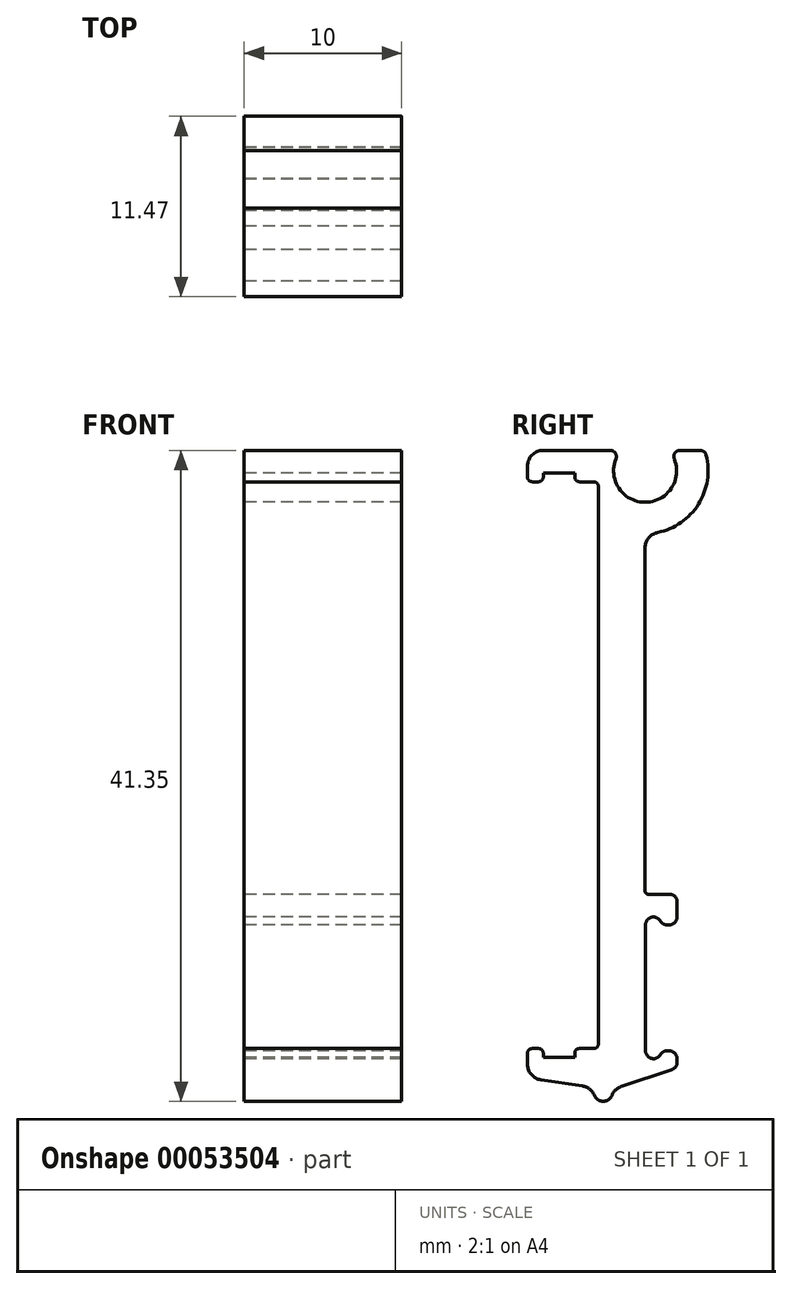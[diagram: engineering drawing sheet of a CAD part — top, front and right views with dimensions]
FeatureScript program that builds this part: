
annotation { "Feature Type Name" : "Feature", "Feature Type Description" : "" }
export const myFeature = defineFeature(function(context is Context, id is Id, definition is map)
    precondition{}
    {
        {
            var Q0;
            Q0=qCreatedBy(makeId("Right.planeOp"),FACE);
            var sketch = newSketch(context, id + "F0", { "sketchPlane" : qUnion([Q0])});
            skLineSegment(sketch, "E0.bottom", {"start": v(9.1, 40) * mm, "end": v(409.1, 40) * mm});
            skLineSegment(sketch, "E0.top", {"start": v(9.1, 21) * mm, "end": v(409.1, 21) * mm});
            skLineSegment(sketch, "E0.left", {"start": v(9.1, 40) * mm, "end": v(9.1, 21) * mm});
            skLineSegment(sketch, "E0.right", {"start": v(409.1, 40) * mm, "end": v(409.1, 21) * mm});
            skSolve(sketch);
        }
        {
            var Q0;
            Q0=qCreatedBy(makeId("Right.planeOp"),FACE);
            var sketch = newSketch(context, id + "F1", { "sketchPlane" : qUnion([Q0])});
            skLineSegment(sketch, "E1.bottom", {"start": v(-0.5, 35) * mm, "end": v(-4.5, 35) * mm});
            skLineSegment(sketch, "E1.top", {"start": v(-0.5, 0) * mm, "end": v(-4.5, 0) * mm});
            skLineSegment(sketch, "E1.left", {"start": v(0, 34.5) * mm, "end": v(0, 0.5) * mm});
            skLineSegment(sketch, "E1.right", {"start": v(-5, 34.5) * mm, "end": v(-5, 0.5) * mm});
            skPoint(sketch, "E2.visualSharp", {"position": v(0, 35) * mm});
            skArc(sketch, "E2.filletArc", {"start": v(0, 34.5) * mm, "mid": v(-0.15, 34.85) * mm, "end": v(-0.5, 35) * mm});
            skPoint(sketch, "E3.visualSharp", {"position": v(-5, 35) * mm});
            skArc(sketch, "E3.filletArc", {"start": v(-4.5, 35) * mm, "mid": v(-4.85, 34.85) * mm, "end": v(-5, 34.5) * mm});
            skPoint(sketch, "E4.visualSharp", {"position": v(-5, 0) * mm});
            skArc(sketch, "E4.filletArc", {"start": v(-5, 0.5) * mm, "mid": v(-4.85, 0.15) * mm, "end": v(-4.5, 0) * mm});
            skPoint(sketch, "E5.visualSharp", {"position": v(0, 0) * mm});
            skArc(sketch, "E5.filletArc", {"start": v(-0.5, 0) * mm, "mid": v(-0.15, 0.15) * mm, "end": v(0, 0.5) * mm});
            skLineSegment(sketch, "E6", {"start": v(-5, 17.5) * mm, "end": v(0, 17.5) * mm, "construction": true});
            skLineSegment(sketch, "E7.rect.bottom", {"start": v(-2.5, 36) * mm, "end": v(-2.5, 36) * mm});
            skLineSegment(sketch, "E7.rect.top", {"start": v(-1.5, 34) * mm, "end": v(-3.5, 34) * mm, "construction": true});
            skLineSegment(sketch, "E7.rect.left", {"start": v(-1.5, 35) * mm, "end": v(-1.5, 34) * mm, "construction": true});
            skLineSegment(sketch, "E7.rect.right", {"start": v(-3.5, 35) * mm, "end": v(-3.5, 34) * mm, "construction": true});
            skPoint(sketch, "E7.rect.middle", {"position": v(-2.5, 35) * mm});
            skPoint(sketch, "E8.visualSharp", {"position": v(-3.5, 36) * mm});
            skArc(sketch, "E8.filletArc", {"start": v(-2.5, 36) * mm, "mid": v(-3.2, 35.7) * mm, "end": v(-3.5, 35) * mm, "construction": true});
            skPoint(sketch, "E9.visualSharp", {"position": v(-1.5, 36) * mm});
            skArc(sketch, "E9.filletArc", {"start": v(-1.5, 35) * mm, "mid": v(-1.8, 35.7) * mm, "end": v(-2.5, 36) * mm, "construction": true});
            skPoint(sketch, "E10.MirrorP", {"position": v(-2.5, 0) * mm});
            skPoint(sketch, "E11.MirrorP", {"position": v(-1.5, -1) * mm});
            skArc(sketch, "E12.MirrorCS", {"start": v(-1.5, 0) * mm, "mid": v(-1.8, -0.7) * mm, "end": v(-2.5, -1) * mm, "construction": true});
            skPoint(sketch, "E13.MirrorP", {"position": v(-3.5, -1) * mm});
            skLineSegment(sketch, "E14.MirrorCS", {"start": v(-2.5, -1) * mm, "end": v(-2.5, -1) * mm});
            skArc(sketch, "E15.MirrorCS", {"start": v(-2.5, -1) * mm, "mid": v(-3.2, -0.7) * mm, "end": v(-3.5, 0) * mm, "construction": true});
            skLineSegment(sketch, "E16.MirrorCS", {"start": v(-3.5, 0) * mm, "end": v(-3.5, 1) * mm, "construction": true});
            skLineSegment(sketch, "E17.MirrorCS", {"start": v(-1.5, 1) * mm, "end": v(-3.5, 1) * mm, "construction": true});
            skLineSegment(sketch, "E18.MirrorCS", {"start": v(-1.5, 0) * mm, "end": v(-1.5, 1) * mm, "construction": true});
            skLineSegment(sketch, "E19.rect.bottom", {"start": v(-4.5, 29.4) * mm, "end": v(-5, 29.4) * mm});
            skLineSegment(sketch, "E19.rect.top", {"start": v(-4.5, 5.6) * mm, "end": v(-5, 5.6) * mm});
            skLineSegment(sketch, "E19.rect.left", {"start": v(-4.5, 29.4) * mm, "end": v(-4.5, 5.6) * mm, "construction": true});
            skPoint(sketch, "E19.rect.middle", {"position": v(-5, 17.5) * mm});
            skPoint(sketch, "E19.rect.right.end.orphan", {"position": v(-5.5, 5.6) * mm});
            skPoint(sketch, "E19.rect.right.start.orphan", {"position": v(-5.5, 29.4) * mm});
            skSolve(sketch);
        }
        {
            var Q0;
            Q0=qCreatedBy(makeId("Right.planeOp"),FACE);
            var sketch = newSketch(context, id + "F2", { "sketchPlane" : qUnion([Q0])});
            skLineSegment(sketch, "E20", {"start": v(-4.2, 35.5) * mm, "end": v(-3.8, 35.5) * mm});
            skLineSegment(sketch, "E21", {"start": v(0, 35.2) * mm, "end": v(0, -0.2) * mm});
            skLineSegment(sketch, "E22", {"start": v(-0.3, -0.5) * mm, "end": v(-1.2, -0.5) * mm});
            skLineSegment(sketch, "E23", {"start": v(-4.5, -0.8) * mm, "end": v(-4.5, -1.5) * mm});
            skLineSegment(sketch, "E24", {"start": v(-3.5, -2.5) * mm, "end": v(2.68, -2.5) * mm, "construction": true});
            skLineSegment(sketch, "E25", {"start": v(-4.5, 35.8) * mm, "end": v(-4.5, 36.5) * mm});
            skLineSegment(sketch, "E26", {"start": v(-3.5, 37.5) * mm, "end": v(0.74, 37.5) * mm});
            skLineSegment(sketch, "E27", {"start": v(-3.5, 35.8) * mm, "end": v(-3.5, 36.05) * mm});
            skLineSegment(sketch, "E28", {"start": v(-3.5, 36.05) * mm, "end": v(-1.5, 36.05) * mm});
            skLineSegment(sketch, "E29", {"start": v(-1.5, 36.05) * mm, "end": v(-1.5, 35.8) * mm});
            skLineSegment(sketch, "E30.trimOffspring", {"start": v(-1.2, 35.5) * mm, "end": v(-0.3, 35.5) * mm});
            skLineSegment(sketch, "E31.MirrorCS", {"start": v(-1.5, -1.05) * mm, "end": v(-1.5, -0.8) * mm});
            skLineSegment(sketch, "E32.MirrorCS", {"start": v(-3.5, -0.8) * mm, "end": v(-3.5, -1.05) * mm});
            skLineSegment(sketch, "E33.MirrorCS", {"start": v(-3.5, -1.05) * mm, "end": v(-1.5, -1.05) * mm});
            skLineSegment(sketch, "E34.trimOffspring", {"start": v(-3.8, -0.5) * mm, "end": v(-4.2, -0.5) * mm});
            skPoint(sketch, "E35.visualSharp", {"position": v(-4.5, 35.5) * mm});
            skArc(sketch, "E35.filletArc", {"start": v(-4.5, 35.8) * mm, "mid": v(-4.41, 35.59) * mm, "end": v(-4.2, 35.5) * mm});
            skPoint(sketch, "E36.visualSharp", {"position": v(-3.5, 35.5) * mm});
            skArc(sketch, "E36.filletArc", {"start": v(-3.8, 35.5) * mm, "mid": v(-3.59, 35.59) * mm, "end": v(-3.5, 35.8) * mm});
            skPoint(sketch, "E37.visualSharp", {"position": v(0, 35.5) * mm});
            skArc(sketch, "E37.filletArc", {"start": v(0, 35.2) * mm, "mid": v(-0.09, 35.41) * mm, "end": v(-0.3, 35.5) * mm});
            skPoint(sketch, "E38.visualSharp", {"position": v(-1.5, 35.5) * mm});
            skArc(sketch, "E38.filletArc", {"start": v(-1.5, 35.8) * mm, "mid": v(-1.41, 35.59) * mm, "end": v(-1.2, 35.5) * mm});
            skPoint(sketch, "E39.visualSharp", {"position": v(-4.5, -0.5) * mm});
            skArc(sketch, "E39.filletArc", {"start": v(-4.2, -0.5) * mm, "mid": v(-4.41, -0.59) * mm, "end": v(-4.5, -0.8) * mm});
            skPoint(sketch, "E40.visualSharp", {"position": v(-3.5, -0.5) * mm});
            skArc(sketch, "E40.filletArc", {"start": v(-3.5, -0.8) * mm, "mid": v(-3.59, -0.59) * mm, "end": v(-3.8, -0.5) * mm});
            skPoint(sketch, "E41.visualSharp", {"position": v(-1.5, -0.5) * mm});
            skArc(sketch, "E41.filletArc", {"start": v(-1.2, -0.5) * mm, "mid": v(-1.41, -0.59) * mm, "end": v(-1.5, -0.8) * mm});
            skPoint(sketch, "E42.visualSharp", {"position": v(0, -0.5) * mm});
            skArc(sketch, "E42.filletArc", {"start": v(-0.3, -0.5) * mm, "mid": v(-0.09, -0.41) * mm, "end": v(0, -0.2) * mm});
            skArc(sketch, "E43", {"start": v(1.11, 36.95) * mm, "mid": v(2.97, 34.2) * mm, "end": v(4.82, 36.95) * mm});
            skArc(sketch, "E44", {"start": v(3.77, 32.28) * mm, "mid": v(6.36, 34.08) * mm, "end": v(6.84, 37.2) * mm});
            skPoint(sketch, "E45.visualSharp", {"position": v(1.45, 37.5) * mm});
            skArc(sketch, "E45.filletArc", {"start": v(1.11, 36.95) * mm, "mid": v(1.07, 37.32) * mm, "end": v(0.74, 37.5) * mm});
            skPoint(sketch, "E46.visualSharp", {"position": v(2.97, 32.2) * mm});
            skArc(sketch, "E46.filletArc", {"start": v(3.77, 32.28) * mm, "mid": v(3.2, 31.93) * mm, "end": v(2.97, 31.3) * mm});
            skPoint(sketch, "E47.visualSharp", {"position": v(-4.5, 37.5) * mm});
            skArc(sketch, "E47.filletArc", {"start": v(-3.5, 37.5) * mm, "mid": v(-4.2, 37.2) * mm, "end": v(-4.5, 36.5) * mm});
            skPoint(sketch, "E48.visualSharp", {"position": v(-4.5, -2.5) * mm});
            skArc(sketch, "E48.filletArc", {"start": v(-4.5, -1.5) * mm, "mid": v(-4.26, -2.15) * mm, "end": v(-3.65, -2.49) * mm});
            skArc(sketch, "E49", {"start": v(4.02, -3.14) * mm, "mid": v(-6.12, -2.09) * mm, "end": v(-15.65, 1.53) * mm, "construction": true});
            skLineSegment(sketch, "E50", {"start": v(-3.65, -2.49) * mm, "end": v(-1.02, -2.88) * mm});
            skArc(sketch, "E51", {"start": v(-0.25, -3.48) * mm, "mid": v(0.31, -3.85) * mm, "end": v(0.86, -3.47) * mm});
            skLineSegment(sketch, "E52", {"start": v(1.48, -2.9) * mm, "end": v(4.66, -1.84) * mm});
            skPoint(sketch, "E53.visualSharp", {"position": v(-0.23, -3) * mm});
            skArc(sketch, "E53.filletArc", {"start": v(-0.25, -3.48) * mm, "mid": v(-0.55, -3.08) * mm, "end": v(-1.02, -2.88) * mm});
            skPoint(sketch, "E54.visualSharp", {"position": v(0.89, -3.1) * mm});
            skArc(sketch, "E54.filletArc", {"start": v(1.48, -2.9) * mm, "mid": v(1.1, -3.12) * mm, "end": v(0.86, -3.47) * mm});
            skPoint(sketch, "E55.visualSharp", {"position": v(2.68, -2.5) * mm});
            skLineSegment(sketch, "E56", {"start": v(6.75, 35) * mm, "end": v(6.75, -7.44) * mm, "construction": true});
            skLineSegment(sketch, "E57", {"start": v(4.5, 9.3) * mm, "end": v(3.17, 9.3) * mm});
            skPoint(sketch, "E58.visualSharp", {"position": v(6.75, 9.3) * mm});
            skLineSegment(sketch, "E59.trimOffspring", {"start": v(2.97, 9.5) * mm, "end": v(2.97, 31.3) * mm});
            skPoint(sketch, "E60.visualSharp", {"position": v(6.75, 6.12) * mm});
            skPoint(sketch, "E61.visualSharp", {"position": v(2.97, 9.3) * mm});
            skArc(sketch, "E61.filletArc", {"start": v(2.97, 9.5) * mm, "mid": v(3.03, 9.36) * mm, "end": v(3.17, 9.3) * mm});
            skLineSegment(sketch, "E62", {"start": v(5, 8.8) * mm, "end": v(5, 7.85) * mm});
            skLineSegment(sketch, "E63", {"start": v(4.5, 7.35) * mm, "end": v(4.37, 7.35) * mm});
            skLineSegment(sketch, "E64", {"start": v(3, 7.35) * mm, "end": v(3, -0.65) * mm});
            skLineSegment(sketch, "E65", {"start": v(4.37, -0.65) * mm, "end": v(4.5, -0.65) * mm});
            skArc(sketch, "E66", {"start": v(3, 7.35) * mm, "mid": v(3.37, 7.84) * mm, "end": v(3.93, 7.6) * mm});
            skArc(sketch, "E67", {"start": v(3, -0.65) * mm, "mid": v(3.37, -1.13) * mm, "end": v(3.93, -0.9) * mm});
            skPoint(sketch, "E68.visualSharp", {"position": v(4, 7.35) * mm});
            skArc(sketch, "E68.filletArc", {"start": v(3.93, 7.6) * mm, "mid": v(4.12, 7.42) * mm, "end": v(4.37, 7.35) * mm});
            skPoint(sketch, "E69.newPointA", {"position": v(5, 7.35) * mm});
            skArc(sketch, "E69.filletArc", {"start": v(4.5, 7.35) * mm, "mid": v(4.85, 7.5) * mm, "end": v(5, 7.85) * mm});
            skPoint(sketch, "E70.visualSharp", {"position": v(4, -0.65) * mm});
            skArc(sketch, "E70.filletArc", {"start": v(4.37, -0.65) * mm, "mid": v(4.12, -0.71) * mm, "end": v(3.93, -0.9) * mm});
            skLineSegment(sketch, "E71", {"start": v(5, -1.15) * mm, "end": v(5, -1.37) * mm});
            skPoint(sketch, "E72.visualSharp", {"position": v(5, -0.65) * mm});
            skArc(sketch, "E72.filletArc", {"start": v(5, -1.15) * mm, "mid": v(4.85, -0.8) * mm, "end": v(4.5, -0.65) * mm});
            skPoint(sketch, "E73.visualSharp", {"position": v(5, -1.73) * mm});
            skArc(sketch, "E73.filletArc", {"start": v(4.66, -1.84) * mm, "mid": v(4.9, -1.66) * mm, "end": v(5, -1.37) * mm});
            skPoint(sketch, "E74.visualSharp", {"position": v(5, 9.3) * mm});
            skArc(sketch, "E74.filletArc", {"start": v(5, 8.8) * mm, "mid": v(4.85, 9.15) * mm, "end": v(4.5, 9.3) * mm});
            skLineSegment(sketch, "E75", {"start": v(5.2, 37.5) * mm, "end": v(6.45, 37.5) * mm});
            skPoint(sketch, "E76.visualSharp", {"position": v(4.49, 37.5) * mm});
            skArc(sketch, "E76.filletArc", {"start": v(5.2, 37.5) * mm, "mid": v(4.86, 37.32) * mm, "end": v(4.82, 36.95) * mm});
            skPoint(sketch, "E77.visualSharp", {"position": v(6.75, 37.5) * mm});
            skArc(sketch, "E77.filletArc", {"start": v(6.84, 37.2) * mm, "mid": v(6.7, 37.42) * mm, "end": v(6.45, 37.5) * mm});
            skSolve(sketch);
        }
        {
            var Q0;
            Q0 = qSketchRegion(id + "F2", true);
            extrude(context, id + "F3", {"entities" : qUnion([Q0]), "depth" : 10 * mm});
        }
    });
